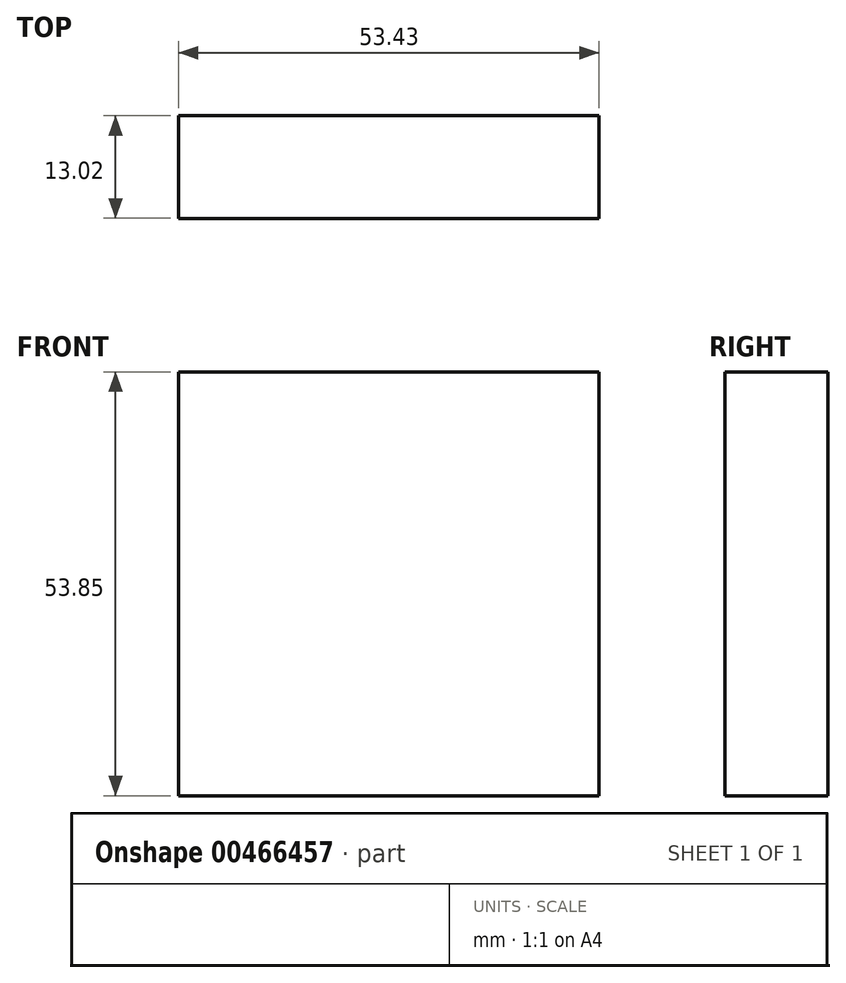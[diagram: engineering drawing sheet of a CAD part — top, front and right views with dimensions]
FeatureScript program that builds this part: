
annotation { "Feature Type Name" : "Feature", "Feature Type Description" : "" }
export const myFeature = defineFeature(function(context is Context, id is Id, definition is map)
    precondition{}
    {
        {
            var Q0;
            Q0=qCreatedBy(makeId("Top.planeOp"),FACE);
            var sketch = newSketch(context, id + "F0", { "sketchPlane" : qUnion([Q0])});
            skLineSegment(sketch, "E0.bottom", {"start": v(-6.25, 6.51) * mm, "end": v(47.18, 6.51) * mm});
            skLineSegment(sketch, "E0.top", {"start": v(-6.25, -6.51) * mm, "end": v(47.18, -6.51) * mm});
            skLineSegment(sketch, "E0.left", {"start": v(-6.25, 6.51) * mm, "end": v(-6.25, -6.51) * mm});
            skLineSegment(sketch, "E0.right", {"start": v(47.18, 6.51) * mm, "end": v(47.18, -6.51) * mm});
            skSolve(sketch);
        }
        {
            var Q0;
            Q0=makeQuery(id+"F0.imprint","IMPRINT",FACE,{"disambiguationData":[TD([[makeQuery(id+"F0.imprint","IMPRINT",EDGE,{"derivedFrom":sQuery(id+"F0.wireOp",EDGE,"E0.bottom")}),-1.0]])]});
            extrude(context, id + "F1", {"entities" : qUnion([Q0]), "depth" : 53.85 * mm, "offsetDistance" : 25.4 * mm});
        }
    });
